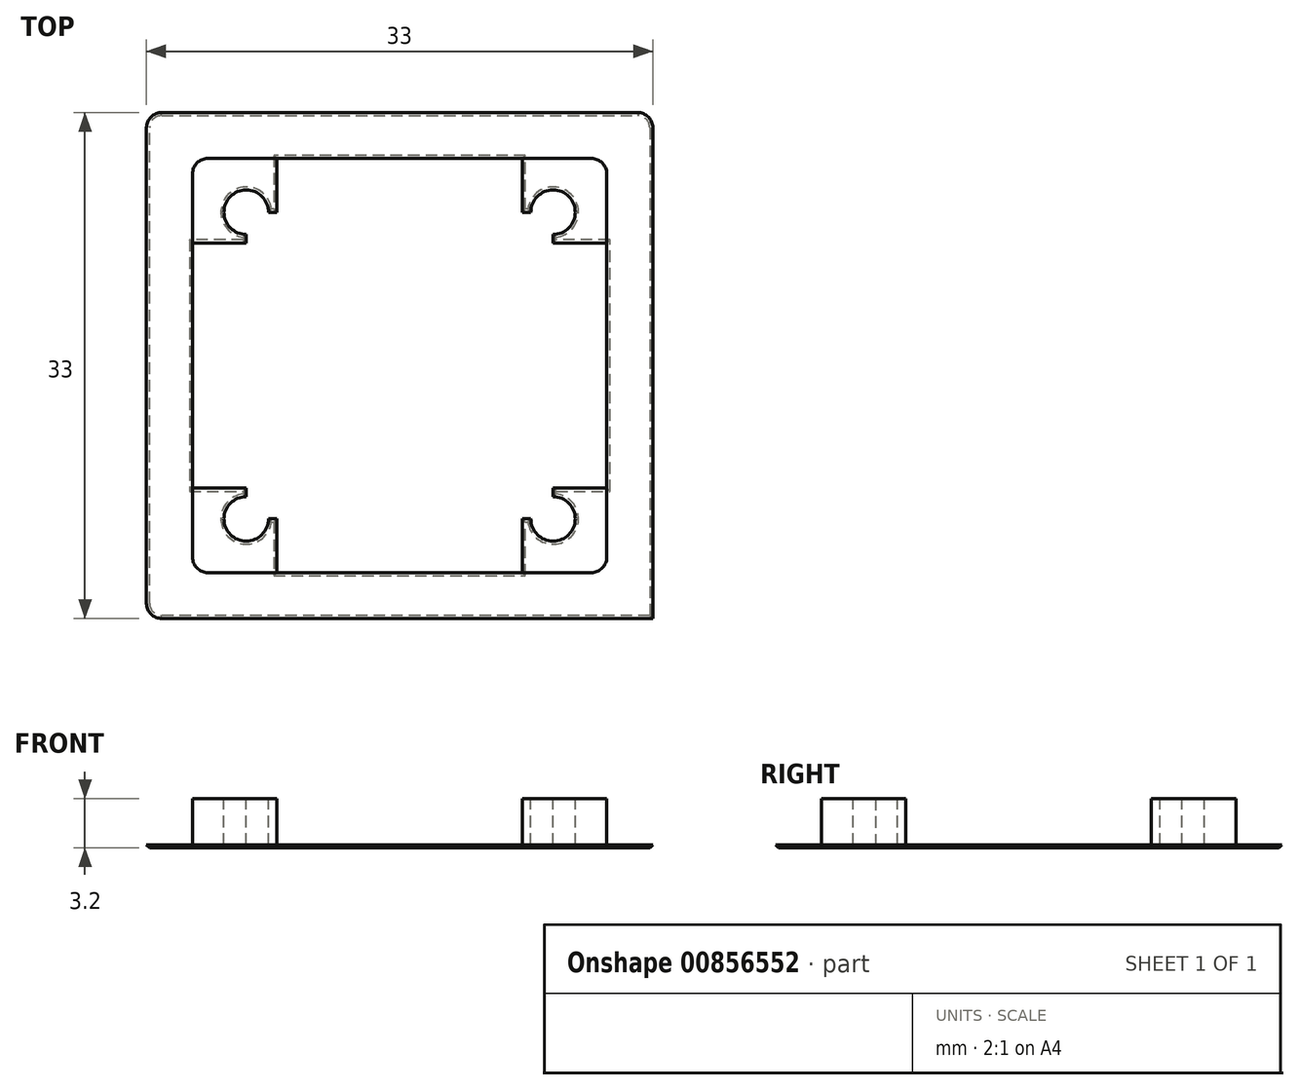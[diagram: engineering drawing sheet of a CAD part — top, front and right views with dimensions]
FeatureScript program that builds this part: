
annotation { "Feature Type Name" : "Feature", "Feature Type Description" : "" }
export const myFeature = defineFeature(function(context is Context, id is Id, definition is map)
    precondition{}
    {
        {
            var Q0;
            Q0=qCreatedBy(makeId("Top.planeOp"),FACE);
            var sketch = newSketch(context, id + "F0", { "sketchPlane" : qUnion([Q0])});
            skLineSegment(sketch, "E0.bottom", {"start": v(10, 10) * mm, "end": v(-10, 10) * mm, "construction": true});
            skLineSegment(sketch, "E0.top", {"start": v(10, -10) * mm, "end": v(-10, -10) * mm, "construction": true});
            skLineSegment(sketch, "E0.left", {"start": v(10, 10) * mm, "end": v(10, -10) * mm, "construction": true});
            skLineSegment(sketch, "E0.right", {"start": v(-10, 10) * mm, "end": v(-10, -10) * mm, "construction": true});
            skPoint(sketch, "E0.middle", {"position": v(0, 0) * mm});
            skCircle(sketch, "E1", {"center": v(10, 10) * mm, "radius": 1.25 * mm, "construction": true});
            skCircle(sketch, "E2.1.0", {"center": v(-10, 10) * mm, "radius": 1.25 * mm, "construction": true});
            skCircle(sketch, "E2.2.0", {"center": v(-10, -10) * mm, "radius": 1.25 * mm, "construction": true});
            skCircle(sketch, "E2.3.0", {"center": v(10, -10) * mm, "radius": 1.25 * mm, "construction": true});
            skLineSegment(sketch, "E3.bottom", {"start": v(13.5, 13.5) * mm, "end": v(-13.5, 13.5) * mm, "construction": true});
            skLineSegment(sketch, "E3.top", {"start": v(13.5, -13.5) * mm, "end": v(-13.5, -13.5) * mm, "construction": true});
            skLineSegment(sketch, "E3.left", {"start": v(13.5, 13.5) * mm, "end": v(13.5, -13.5) * mm, "construction": true});
            skLineSegment(sketch, "E3.right", {"start": v(-13.5, 13.5) * mm, "end": v(-13.5, -13.5) * mm, "construction": true});
            skSolve(sketch);
        }
        {
            var Q0;
            Q0=qCreatedBy(makeId("Top.planeOp"),FACE);
            var sketch = newSketch(context, id + "F1", { "sketchPlane" : qUnion([Q0])});
            skCircle(sketch, "E4.0", {"center": v(10, 10) * mm, "radius": 1.45 * mm});
            skCircle(sketch, "E5.1.0", {"center": v(-10, 10) * mm, "radius": 1.45 * mm});
            skCircle(sketch, "E5.2.0", {"center": v(-10, -10) * mm, "radius": 1.45 * mm});
            skCircle(sketch, "E5.3.0", {"center": v(10, -10) * mm, "radius": 1.45 * mm});
            skPoint(sketch, "E5.center", {"position": v(0, 0) * mm});
            skSolve(sketch);
        }
        {
            var Q0;
            Q0=qCreatedBy(makeId("Front.planeOp"),FACE);
            var sketch = newSketch(context, id + "F2", { "sketchPlane" : qUnion([Q0])});
            skLineSegment(sketch, "E6", {"start": v(0, 0) * mm, "end": v(0, 3) * mm});
            skLineSegment(sketch, "E7", {"start": v(0, 0) * mm, "end": v(0, -0.2) * mm});
            skSolve(sketch);
        }
        {
            var Q0;
            Q0=qCreatedBy(makeId("Top.planeOp"),FACE);
            var sketch = newSketch(context, id + "F3", { "sketchPlane" : qUnion([Q0])});
            skPoint(sketch, "E8.0", {"position": v(10, 10) * mm});
            skArc(sketch, "E9", {"start": v(8, 10) * mm, "mid": v(11.41, 11.41) * mm, "end": v(10, 8) * mm, "construction": true});
            skLineSegment(sketch, "E10.0", {"start": v(13.5, 13.5) * mm, "end": v(-13.5, 13.5) * mm, "construction": true});
            skLineSegment(sketch, "E11.0", {"start": v(13.5, 13.5) * mm, "end": v(13.5, -13.5) * mm, "construction": true});
            skLineSegment(sketch, "E12", {"start": v(8, 10) * mm, "end": v(8, 13.5) * mm});
            skLineSegment(sketch, "E13", {"start": v(8, 13.5) * mm, "end": v(0, 13.5) * mm});
            skLineSegment(sketch, "E14", {"start": v(10, 8) * mm, "end": v(13.5, 8) * mm});
            skLineSegment(sketch, "E15", {"start": v(13.5, 8) * mm, "end": v(13.5, 0) * mm});
            skLineSegment(sketch, "E16", {"start": v(8, 10) * mm, "end": v(10, 10) * mm});
            skLineSegment(sketch, "E17", {"start": v(10, 8) * mm, "end": v(10, 10) * mm});
            skLineSegment(sketch, "E18", {"start": v(0, 16.5) * mm, "end": v(16.5, 16.5) * mm});
            skLineSegment(sketch, "E19", {"start": v(16.5, 16.5) * mm, "end": v(16.5, 0) * mm});
            skLineSegment(sketch, "E20", {"start": v(8, 13.5) * mm, "end": v(13.5, 13.5) * mm});
            skLineSegment(sketch, "E21", {"start": v(13.5, 13.5) * mm, "end": v(13.5, 8) * mm});
            skLineSegment(sketch, "E22.1.0", {"start": v(-16.5, 0) * mm, "end": v(-16.5, 16.5) * mm});
            skLineSegment(sketch, "E22.1.1", {"start": v(-10, 8) * mm, "end": v(-13.5, 8) * mm});
            skLineSegment(sketch, "E22.1.2", {"start": v(-13.5, 8) * mm, "end": v(-13.5, 0) * mm});
            skLineSegment(sketch, "E22.1.3", {"start": v(-8, 10) * mm, "end": v(-8, 13.5) * mm});
            skPoint(sketch, "E22.1.4", {"position": v(-10, 10) * mm});
            skLineSegment(sketch, "E22.1.5", {"start": v(-16.5, 16.5) * mm, "end": v(0, 16.5) * mm});
            skLineSegment(sketch, "E22.1.6", {"start": v(-13.5, 8) * mm, "end": v(-13.5, 13.5) * mm});
            skArc(sketch, "E22.1.7", {"start": v(-10, 8) * mm, "mid": v(-11.41, 11.41) * mm, "end": v(-8, 10) * mm, "construction": true});
            skLineSegment(sketch, "E22.1.8", {"start": v(-8, 13.5) * mm, "end": v(0, 13.5) * mm});
            skLineSegment(sketch, "E22.1.9", {"start": v(-13.5, 13.5) * mm, "end": v(-8, 13.5) * mm});
            skLineSegment(sketch, "E22.1.10", {"start": v(-8, 10) * mm, "end": v(-10, 10) * mm});
            skLineSegment(sketch, "E22.1.11", {"start": v(-10, 8) * mm, "end": v(-10, 10) * mm});
            skLineSegment(sketch, "E22.2.0", {"start": v(0, -16.5) * mm, "end": v(-16.5, -16.5) * mm});
            skLineSegment(sketch, "E22.2.1", {"start": v(-8, -10) * mm, "end": v(-8, -13.5) * mm});
            skLineSegment(sketch, "E22.2.2", {"start": v(-8, -13.5) * mm, "end": v(0, -13.5) * mm});
            skLineSegment(sketch, "E22.2.3", {"start": v(-10, -8) * mm, "end": v(-13.5, -8) * mm});
            skPoint(sketch, "E22.2.4", {"position": v(-10, -10) * mm});
            skLineSegment(sketch, "E22.2.5", {"start": v(-16.5, -16.5) * mm, "end": v(-16.5, 0) * mm});
            skLineSegment(sketch, "E22.2.6", {"start": v(-8, -13.5) * mm, "end": v(-13.5, -13.5) * mm});
            skArc(sketch, "E22.2.7", {"start": v(-8, -10) * mm, "mid": v(-11.41, -11.41) * mm, "end": v(-10, -8) * mm, "construction": true});
            skLineSegment(sketch, "E22.2.8", {"start": v(-13.5, -8) * mm, "end": v(-13.5, 0) * mm});
            skLineSegment(sketch, "E22.2.9", {"start": v(-13.5, -13.5) * mm, "end": v(-13.5, -8) * mm});
            skLineSegment(sketch, "E22.2.10", {"start": v(-10, -8) * mm, "end": v(-10, -10) * mm});
            skLineSegment(sketch, "E22.2.11", {"start": v(-8, -10) * mm, "end": v(-10, -10) * mm});
            skLineSegment(sketch, "E22.3.0", {"start": v(16.5, 0) * mm, "end": v(16.5, -16.5) * mm});
            skLineSegment(sketch, "E22.3.1", {"start": v(10, -8) * mm, "end": v(13.5, -8) * mm});
            skLineSegment(sketch, "E22.3.2", {"start": v(13.5, -8) * mm, "end": v(13.5, 0) * mm});
            skLineSegment(sketch, "E22.3.3", {"start": v(8, -10) * mm, "end": v(8, -13.5) * mm});
            skPoint(sketch, "E22.3.4", {"position": v(10, -10) * mm});
            skLineSegment(sketch, "E22.3.5", {"start": v(16.5, -16.5) * mm, "end": v(0, -16.5) * mm});
            skLineSegment(sketch, "E22.3.6", {"start": v(13.5, -8) * mm, "end": v(13.5, -13.5) * mm});
            skArc(sketch, "E22.3.7", {"start": v(10, -8) * mm, "mid": v(11.41, -11.41) * mm, "end": v(8, -10) * mm, "construction": true});
            skLineSegment(sketch, "E22.3.8", {"start": v(8, -13.5) * mm, "end": v(0, -13.5) * mm});
            skLineSegment(sketch, "E22.3.9", {"start": v(13.5, -13.5) * mm, "end": v(8, -13.5) * mm});
            skLineSegment(sketch, "E22.3.10", {"start": v(8, -10) * mm, "end": v(10, -10) * mm});
            skLineSegment(sketch, "E22.3.11", {"start": v(10, -8) * mm, "end": v(10, -10) * mm});
            skPoint(sketch, "E22.center", {"position": v(0, 0) * mm});
            skSolve(sketch);
        }
        {
            var Q0;
            Q0=makeQuery(id+"F3.imprint","IMPRINT",FACE,{"disambiguationData":[TD([[makeQuery(id+"F3.imprint","IMPRINT",EDGE,{"derivedFrom":sQuery(id+"F3.wireOp",EDGE,"E13")}),-1.0]])]});
            var Q1;
            Q1=makeQuery(id+"F3.imprint","IMPRINT",FACE,{"disambiguationData":[TD([[makeQuery(id+"F3.imprint","IMPRINT",EDGE,{"derivedFrom":sQuery(id+"F3.wireOp",EDGE,"E22.2.1")}),-1.0]])]});
            var Q2;
            Q2=makeQuery(id+"F3.imprint","IMPRINT",FACE,{"disambiguationData":[TD([[makeQuery(id+"F3.imprint","IMPRINT",EDGE,{"derivedFrom":sQuery(id+"F3.wireOp",EDGE,"E22.1.1")}),-1.0]])]});
            var Q3;
            Q3=makeQuery(id+"F3.imprint","IMPRINT",FACE,{"disambiguationData":[TD([[makeQuery(id+"F3.imprint","IMPRINT",EDGE,{"derivedFrom":sQuery(id+"F3.wireOp",EDGE,"E12")}),-1.0]])]});
            var Q4;
            Q4=makeQuery(id+"F3.imprint","IMPRINT",FACE,{"disambiguationData":[TD([[makeQuery(id+"F3.imprint","IMPRINT",EDGE,{"derivedFrom":sQuery(id+"F3.wireOp",EDGE,"E22.3.1")}),-1.0]])]});
            var Q5;
            Q5=sQuery(id+"F2.wireOp",EDGE,"E7");
            sweep(context, id + "F4", {"profiles" : qUnion([Q0, Q1, Q2, Q3, Q4]), "path" : qUnion([Q5])});
        }
        {
            var Q0;
            Q0=makeQuery(id+"F3.imprint","IMPRINT",FACE,{"disambiguationData":[TD([[makeQuery(id+"F3.imprint","IMPRINT",EDGE,{"derivedFrom":sQuery(id+"F3.wireOp",EDGE,"E22.1.1")}),-1.0]])]});
            var Q1;
            Q1=makeQuery(id+"F3.imprint","IMPRINT",FACE,{"disambiguationData":[TD([[makeQuery(id+"F3.imprint","IMPRINT",EDGE,{"derivedFrom":sQuery(id+"F3.wireOp",EDGE,"E12")}),-1.0]])]});
            var Q2;
            Q2=makeQuery(id+"F3.imprint","IMPRINT",FACE,{"disambiguationData":[TD([[makeQuery(id+"F3.imprint","IMPRINT",EDGE,{"derivedFrom":sQuery(id+"F3.wireOp",EDGE,"E22.2.1")}),-1.0]])]});
            var Q3;
            Q3=makeQuery(id+"F3.imprint","IMPRINT",FACE,{"disambiguationData":[TD([[makeQuery(id+"F3.imprint","IMPRINT",EDGE,{"derivedFrom":sQuery(id+"F3.wireOp",EDGE,"E22.3.1")}),-1.0]])]});
            var Q4;
            Q4=sQuery(id+"F2.wireOp",EDGE,"E6");
            sweep(context, id + "F5", {"operationType" : NewBodyOperationType.ADD, "profiles" : qUnion([Q0, Q1, Q2, Q3]), "path" : qUnion([Q4])});
        }
        {
            var Q0;
            Q0 = qSketchRegion(id + "F1", true);
            extrude(context, id + "F6", {"entities" : qUnion([Q0]), "operationType" : NewBodyOperationType.REMOVE, "endBound" : BoundingType.THROUGH_ALL, "oppositeDirection" : true, "depth" : 25 * mm, "offsetDistance" : 25 * mm, "hasSecondDirection" : true, "secondDirectionBound" : SecondDirectionBoundingType.THROUGH_ALL, "secondDirectionOppositeDirection" : false, "secondDirectionDepth" : 25 * mm});
        }
        {
            var Q0;
            Q0=makeQuery(id+"F4.opSweep","SWEPT_EDGE",EDGE,{"disambiguationData":[OSD([sQuery(id+"F2.wireOp",EDGE,"E7"),sQuery(id+"F3.wireOp",EDGE,"E18"),sQuery(id+"F3.wireOp",EDGE,"E19")])]});
            var Q1;
            Q1=makeQuery(id+"F5.opSweep","SWEPT_EDGE",EDGE,{"disambiguationData":[OSD([sQuery(id+"F2.wireOp",EDGE,"E6"),sQuery(id+"F3.wireOp",EDGE,"E22.3.6"),sQuery(id+"F3.wireOp",EDGE,"E22.3.9")])]});
            var Q2;
            Q2=makeQuery(id+"F5.opSweep","SWEPT_EDGE",EDGE,{"disambiguationData":[OSD([sQuery(id+"F2.wireOp",EDGE,"E6"),sQuery(id+"F3.wireOp",EDGE,"E20"),sQuery(id+"F3.wireOp",EDGE,"E21")])]});
            var Q3;
            Q3=makeQuery(id+"F5.opSweep","SWEPT_EDGE",EDGE,{"disambiguationData":[OSD([sQuery(id+"F2.wireOp",EDGE,"E6"),sQuery(id+"F3.wireOp",EDGE,"E22.2.6"),sQuery(id+"F3.wireOp",EDGE,"E22.2.9")])]});
            var Q4;
            Q4=makeQuery(id+"F4.opSweep","SWEPT_EDGE",EDGE,{"disambiguationData":[OSD([sQuery(id+"F2.wireOp",EDGE,"E7"),sQuery(id+"F3.wireOp",EDGE,"E22.2.0"),sQuery(id+"F3.wireOp",EDGE,"E22.2.5")])]});
            var Q5;
            Q5=makeQuery(id+"F5.opSweep","SWEPT_EDGE",EDGE,{"disambiguationData":[OSD([sQuery(id+"F2.wireOp",EDGE,"E6"),sQuery(id+"F3.wireOp",EDGE,"E22.1.6"),sQuery(id+"F3.wireOp",EDGE,"E22.1.9")])]});
            var Q6;
            Q6=makeQuery(id+"F4.opSweep","SWEPT_EDGE",EDGE,{"disambiguationData":[OSD([sQuery(id+"F2.wireOp",EDGE,"E7"),sQuery(id+"F3.wireOp",EDGE,"E22.1.0"),sQuery(id+"F3.wireOp",EDGE,"E22.1.5")])]});
            fillet(context, id + "F7", {"entities" : qUnion([Q0, Q1, Q2, Q3, Q4, Q5, Q6]), "radius" : 1 * mm, "allowEdgeOverflow" : false});
        }
        {
            var Q0;
            Q0=makeQuery(id+"F4.opSweep","CAP_FACE",FACE,{"disambiguationData":[OSD([sQuery(id+"F2.wireOp",VERTEX,"E7.end"),sQuery(id+"F3.wireOp",EDGE,"E12"),sQuery(id+"F3.wireOp",EDGE,"E13"),sQuery(id+"F3.wireOp",EDGE,"E14"),sQuery(id+"F3.wireOp",EDGE,"E15"),sQuery(id+"F3.wireOp",EDGE,"E16"),sQuery(id+"F3.wireOp",EDGE,"E17"),sQuery(id+"F3.wireOp",EDGE,"E18"),sQuery(id+"F3.wireOp",EDGE,"E19"),sQuery(id+"F3.wireOp",EDGE,"E22.1.0"),sQuery(id+"F3.wireOp",EDGE,"E22.1.1"),sQuery(id+"F3.wireOp",EDGE,"E22.1.2"),sQuery(id+"F3.wireOp",EDGE,"E22.1.3"),sQuery(id+"F3.wireOp",EDGE,"E22.1.5"),sQuery(id+"F3.wireOp",EDGE,"E22.1.8"),sQuery(id+"F3.wireOp",EDGE,"E22.1.10"),sQuery(id+"F3.wireOp",EDGE,"E22.1.11"),sQuery(id+"F3.wireOp",EDGE,"E22.2.0"),sQuery(id+"F3.wireOp",EDGE,"E22.2.1"),sQuery(id+"F3.wireOp",EDGE,"E22.2.2"),sQuery(id+"F3.wireOp",EDGE,"E22.2.3"),sQuery(id+"F3.wireOp",EDGE,"E22.2.5"),sQuery(id+"F3.wireOp",EDGE,"E22.2.8"),sQuery(id+"F3.wireOp",EDGE,"E22.2.10"),sQuery(id+"F3.wireOp",EDGE,"E22.2.11"),sQuery(id+"F3.wireOp",EDGE,"E22.3.0"),sQuery(id+"F3.wireOp",EDGE,"E22.3.1"),sQuery(id+"F3.wireOp",EDGE,"E22.3.2"),sQuery(id+"F3.wireOp",EDGE,"E22.3.3"),sQuery(id+"F3.wireOp",EDGE,"E22.3.5"),sQuery(id+"F3.wireOp",EDGE,"E22.3.8"),sQuery(id+"F3.wireOp",EDGE,"E22.3.10"),sQuery(id+"F3.wireOp",EDGE,"E22.3.11")])],"isStart":false});
            chamfer(context, id + "F8", {"entities" : qUnion([Q0]), "width" : 0.2 * mm});
        }
    });
